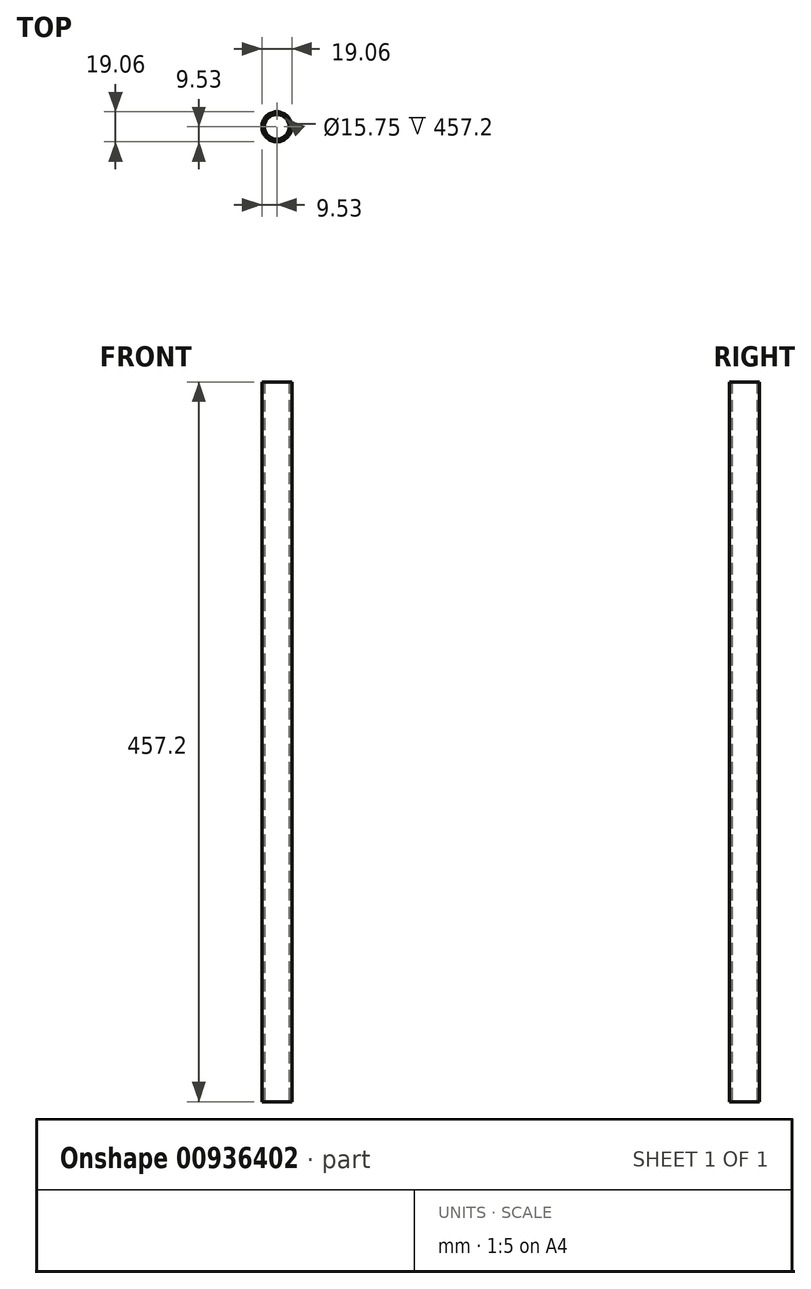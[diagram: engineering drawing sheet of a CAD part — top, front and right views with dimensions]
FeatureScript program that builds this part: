
annotation { "Feature Type Name" : "Feature", "Feature Type Description" : "" }
export const myFeature = defineFeature(function(context is Context, id is Id, definition is map)
    precondition{}
    {
        {
            var Q0;
            Q0=qCreatedBy(makeId("Top.planeOp"),FACE);
            var sketch = newSketch(context, id + "F0", { "sketchPlane" : qUnion([Q0])});
            skCircle(sketch, "E0", {"center": v(0, 0) * mm, "radius": 9.53 * mm});
            skCircle(sketch, "E1", {"center": v(0, 0) * mm, "radius": 7.87 * mm});
            skSolve(sketch);
        }
        {
            var Q0;
            Q0=makeQuery(id+"F0.imprint","IMPRINT",FACE,{"disambiguationData":[TD([[makeQuery(id+"F0.imprint","IMPRINT",EDGE,{"derivedFrom":sQuery(id+"F0.wireOp",EDGE,"E0")}),1.0]])]});
            extrude(context, id + "F1", {"entities" : qUnion([Q0]), "depth" : 457.2 * mm, "offsetDistance" : 25.4 * mm});
        }
    });
